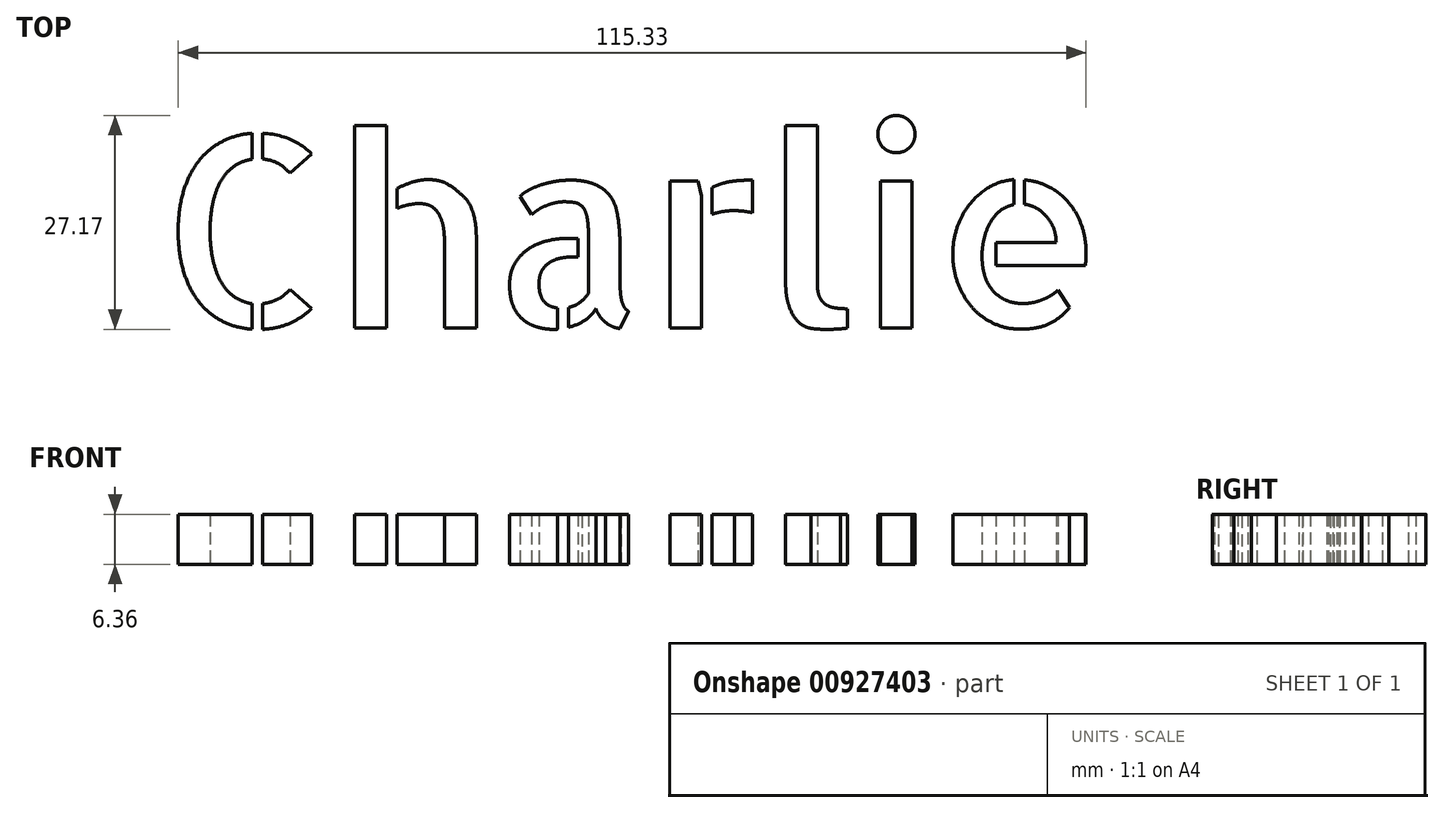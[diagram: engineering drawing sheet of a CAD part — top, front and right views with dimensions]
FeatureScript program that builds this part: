
annotation { "Feature Type Name" : "Feature", "Feature Type Description" : "" }
export const myFeature = defineFeature(function(context is Context, id is Id, definition is map)
    precondition{}
    {
        {
            var Q0;
            Q0=qCreatedBy(makeId("Top.planeOp"),FACE);
            var sketch = newSketch(context, id + "F0", { "sketchPlane" : qUnion([Q0])});
            skText(sketch, "E0", { "text": "Charlie", "fontName": "AllertaStencil-Regular.ttf"});
            const initialGuessF0  = {"E0": [-0.03742, -0.01167, 1, 0, 0.0244]};
            skSetInitialGuess(sketch, initialGuessF0);
            skSolve(sketch);
        }
        {
            var Q0;
            Q0 = qSketchRegion(id + "F0", true);
            extrude(context, id + "F1", {"entities" : qUnion([Q0]), "endBound" : BoundingType.SYMMETRIC, "depth" : 6.35 * mm, "offsetDistance" : 25.4 * mm});
        }
    });
